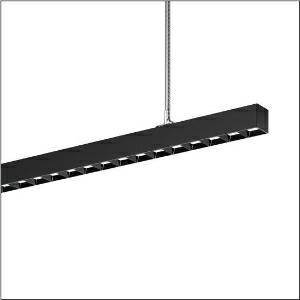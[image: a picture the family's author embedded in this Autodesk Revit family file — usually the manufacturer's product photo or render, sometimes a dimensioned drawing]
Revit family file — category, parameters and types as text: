
# Revit family: silica_21_51mx31dc4dbb
name_source: partatom
category: Lighting Fixtures
units: mm (PartAtom-declared; Revit-internal decimal feet)

## family parameters
Cut with Voids When Loaded = No
Host = Face
Light Source = No
Part Type = Normal
Room Calculation Point = No
Round Connector Dimension = Use Diameter
Shared = No

## types (1)
- --- (1 x LED, 18230 lm, 105.9 W, 4000K)
    Apparent Load = 106 VA
    CIE Flux Codes = 87 99 100 59 100
    Color Rendering = 80
    Color Temperature = 4000K
    Default Elevation = 1800 mm
    Description = Silica 21, office luminaire, primary light control with darklight reflector, of PMMA, black, CAT 2 (L<= 3000cd/m²), light emission: direct/indirect distribution, primary light characteristic: symmetric, installation type: suspended mounting, LED, rated luminous flux: 18.230lm, luminous efficacy: 172lm/W, light colour: 840, colour temperature: 4000K, control gear: DALI 2, with terminal, 3+2-pole, max. 2.5mm², mains connection: 220..240V, AC, 50/60Hz, rated input power: 105.9W, luminaire housing, of aluminium, matt jet black (RAL 9005), length: 3.004mm, width: 53mm, height: 53mm, protection rating (complete): IP20, insulation class (complete): insulation class I (protective earthing), certification: CE, permissible operating ambient temperature: 0..+35°C, standard: EN 50419, packaging unit: 1 piece
    Height = 53 mm
    Lamp = 1 x LED
    Lamp Light Flux = 18230 lm
    Lamp Power = 105.9 W
    Lamp count = 1
    Length = 3004 mm
    Luminous efficacy = 172 lm/W
    Manufacturer = Siteco
    ModVariant = No
    Model = 51MX31DC4DBB
    Mounting Place = Ceiling
    Mounting Type = Pendant
    Number of Poles = 1
    OnlyDefault = Yes
    Power Factor = 1
    Product Name = Silica 21
    Product group = office luminaire | ceiling pendant
    ProductGroupID = 903
    Protection Class = Protection class I
    Protection Degree = IP 20
    RLX_Detail_Level = 1
    RLX_Emergency_Light_Flux = 0 lm
    RLX_Emergency_Type = 0
    RLX_Emergency_Type_DB = No
    RlxData = <blob elided: 66749 chars, md5=d3125239>
    Socket = socket
    Standby Power = 0 W
    System Light Flux = 18230 lm
    System Power = 106 W
    Type Comments = factory setting: luminous flux: 100 % | dim-lin: 254 | 367 mA
    Type Image = l_1335852.jpg
    URL = http://relux.com
    VarID = @adj_121269
    Voltage = 0 V
    Weight = 0.00 kg
    Width = 53 mm

## geometry (parser evidence)
native form markers: Blend x4, Sweep x14
no freeform markers — native parametric forms only
